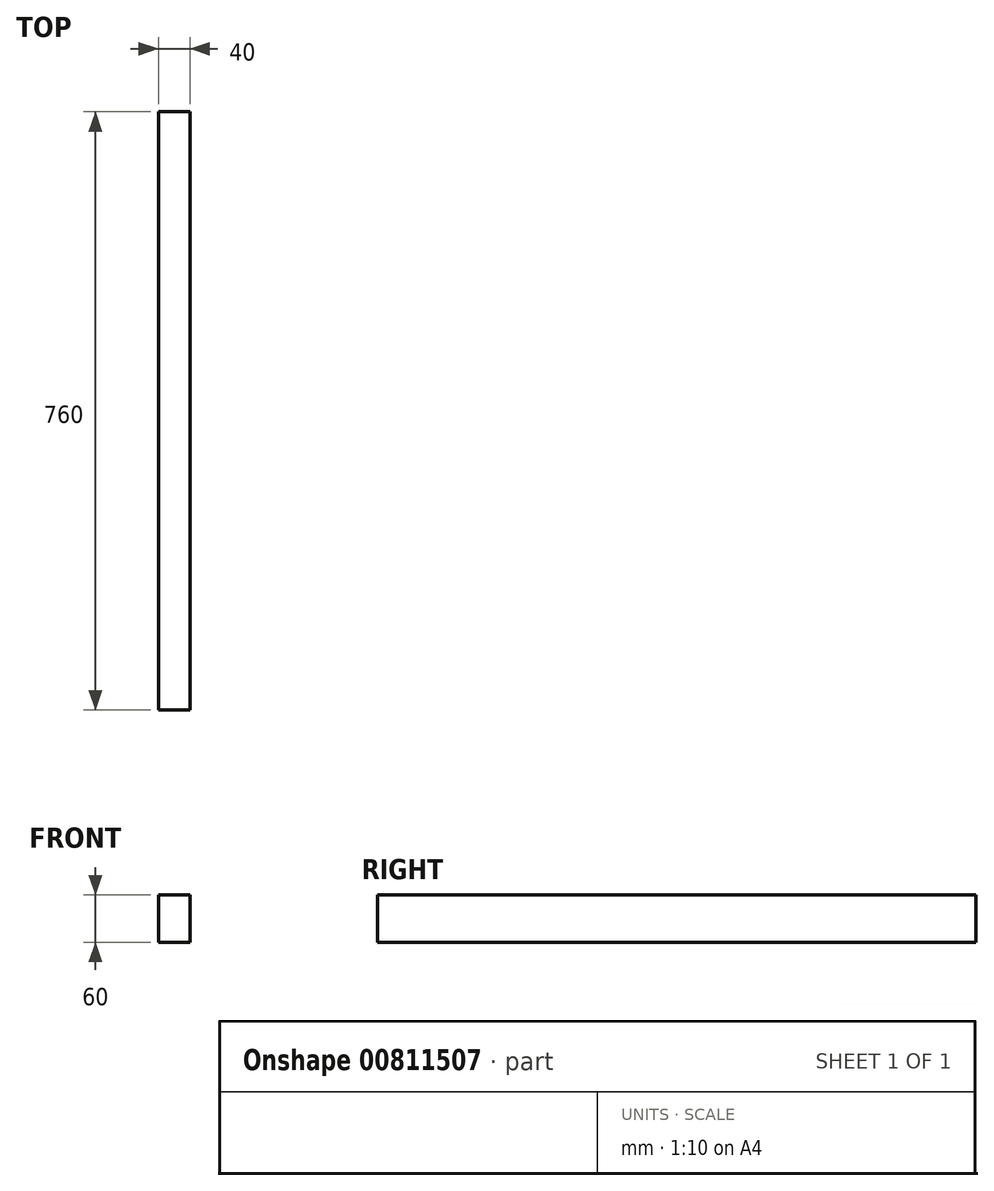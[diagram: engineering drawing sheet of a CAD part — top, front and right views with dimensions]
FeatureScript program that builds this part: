
annotation { "Feature Type Name" : "Feature", "Feature Type Description" : "" }
export const myFeature = defineFeature(function(context is Context, id is Id, definition is map)
    precondition{}
    {
        {
            var Q0;
            Q0=qCreatedBy(makeId("Front.planeOp"),FACE);
            var sketch = newSketch(context, id + "F0", { "sketchPlane" : qUnion([Q0])});
            skLineSegment(sketch, "E0.bottom", {"start": v(20, 30) * mm, "end": v(-20, 30) * mm});
            skLineSegment(sketch, "E0.top", {"start": v(20, -30) * mm, "end": v(-20, -30) * mm});
            skLineSegment(sketch, "E0.left", {"start": v(20, 30) * mm, "end": v(20, -30) * mm});
            skLineSegment(sketch, "E0.right", {"start": v(-20, 30) * mm, "end": v(-20, -30) * mm});
            skPoint(sketch, "E0.middle", {"position": v(0, 0) * mm});
            skSolve(sketch);
        }
        {
            var Q0;
            Q0=makeQuery(id+"F0.imprint","IMPRINT",FACE,{"disambiguationData":[TD([[makeQuery(id+"F0.imprint","IMPRINT",EDGE,{"derivedFrom":sQuery(id+"F0.wireOp",EDGE,"E0.bottom")}),1.0]])]});
            extrude(context, id + "F1", {"entities" : qUnion([Q0]), "endBound" : BoundingType.SYMMETRIC, "depth" : 760 * mm, "offsetDistance" : 25.4 * mm});
        }
    });
